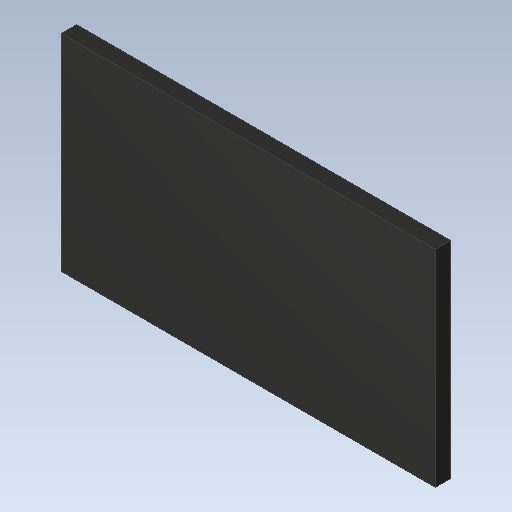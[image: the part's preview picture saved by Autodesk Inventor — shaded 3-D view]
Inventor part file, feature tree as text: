
AUTODESK INVENTOR PART (.ipt)
format: ipt  version: 2023 (Build 270158000, 158)  size: 91,136 bytes
history: imported  units: in
note: dims shown in document units (in); Inventor stores cm internally (conversion verified against a paired STEP export)
features: imported_body x1
ambient origin geometry x8: Origin, YZ Plane, XZ Plane, XY Plane, X Axis, Y Axis, Z Axis, Center Point
bodies: Solid1 (imported_parasolid), Body1 (imported_parasolid)
feature tree (1):
  imported_body  NMx_Import_Brep_tag  [imported B-rep: ~6 faces, bbox_mm=[2.4508, 1.3508, 0.1]]
